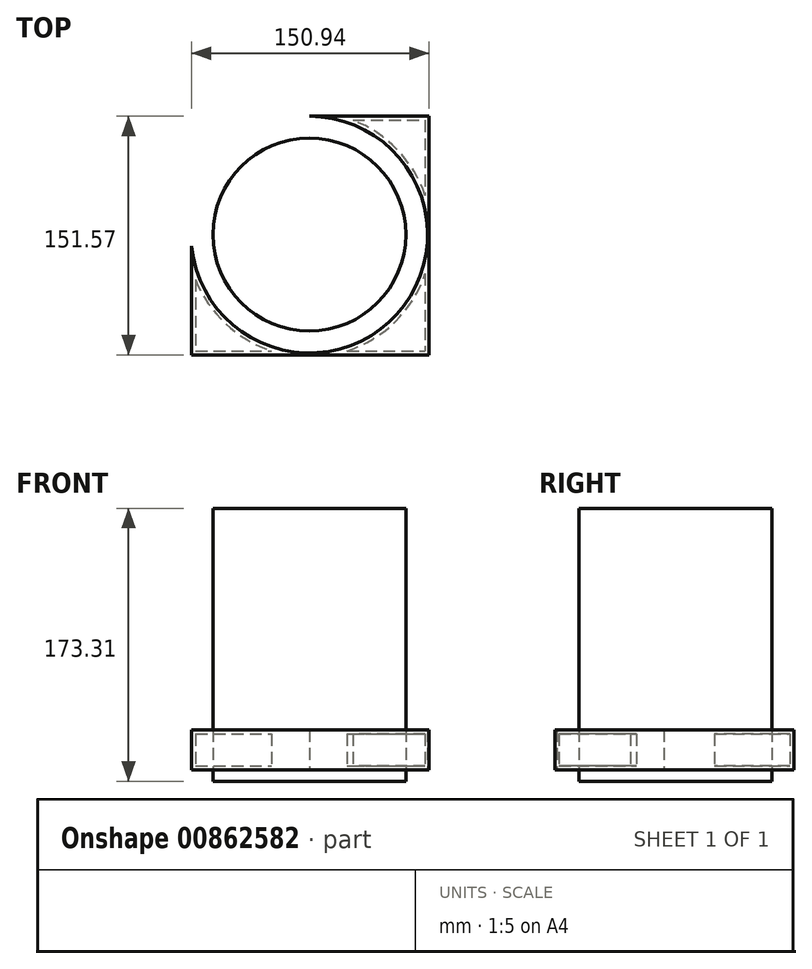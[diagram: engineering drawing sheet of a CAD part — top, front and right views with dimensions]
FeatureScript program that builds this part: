
annotation { "Feature Type Name" : "Feature", "Feature Type Description" : "" }
export const myFeature = defineFeature(function(context is Context, id is Id, definition is map)
    precondition{}
    {
        {
            var Q0;
            Q0=qCreatedBy(makeId("Top.planeOp"),FACE);
            var sketch = newSketch(context, id + "F0", { "sketchPlane" : qUnion([Q0])});
            skLineSegment(sketch, "E0.bottom", {"start": v(-74.79, 75.15) * mm, "end": v(76.15, 75.15) * mm});
            skLineSegment(sketch, "E0.top", {"start": v(-74.79, -76.42) * mm, "end": v(76.15, -76.42) * mm});
            skLineSegment(sketch, "E0.left", {"start": v(-74.79, 75.15) * mm, "end": v(-74.79, -76.42) * mm});
            skLineSegment(sketch, "E0.right", {"start": v(76.15, 75.15) * mm, "end": v(76.15, -76.42) * mm});
            skCircle(sketch, "E1", {"center": v(0, 0) * mm, "radius": 75.15 * mm});
            skSolve(sketch);
        }
        {
            var Q0;
            {var subQ0=sQuery(id+"F0.wireOp",EDGE,"E1");var subQ1=sQuery(id+"F0.wireOp",EDGE,"E0.left");var subQ2=makeQuery(id+"F0.imprint","INTERSECT",VERTEX,{"disambiguationData":[OD(0.0)],"derivedFrom":[subQ1,subQ0]});Q0=makeQuery(id+"F0.imprint","IMPRINT",FACE,{"disambiguationData":[TD([[makeQuery(id+"F0.imprint","IMPRINT",EDGE,{"disambiguationData":[TD([[subQ2,-1.0]])],"derivedFrom":subQ1}),1.0]])]});}
            extrude(context, id + "F1", {"entities" : qUnion([Q0]), "depth" : 25.4 * mm, "offsetDistance" : 25.4 * mm});
        }
        {
            var Q0;
            Q0=makeQuery(id+"F1.opExtrude","CAP_FACE",FACE,{"disambiguationData":[OSD([sQuery(id+"F0.wireOp",EDGE,"E0.left"),sQuery(id+"F0.wireOp",EDGE,"E1")])],"isStart":false});
            var sketch = newSketch(context, id + "F2", { "sketchPlane" : qUnion([Q0])});
            skCircle(sketch, "E2", {"center": v(0, 0) * mm, "radius": 61.24 * mm});
            skSolve(sketch);
        }
        {
            var Q0;
            Q0=makeQuery(id+"F2.imprint","IMPRINT",FACE,{"disambiguationData":[TD([[makeQuery(id+"F2.imprint","IMPRINT",EDGE,{"derivedFrom":sQuery(id+"F2.wireOp",EDGE,"E2")}),1.0]])]});
            extrude(context, id + "F3", {"entities" : qUnion([Q0]), "operationType" : NewBodyOperationType.ADD, "depth" : 140.76 * mm, "offsetDistance" : 25.4 * mm, "hasSecondDirection" : true, "secondDirectionOppositeDirection" : true, "secondDirectionDepth" : 32.55 * mm});
        }
        {
            var Q0;
            {var subQ0=sQuery(id+"F2.wireOp",EDGE,"E2");Q0=makeQuery(id+"F3.boolean.opBoolean","SPLIT",FACE,{"disambiguationData":[TD([makeQuery(id+"F3.opExtrude","CAP_FACE",FACE,{"disambiguationData":[OSD([subQ0])],"isStart":false})])],"derivedFrom":makeQuery(id+"F3.opExtrude","SWEPT_FACE",FACE,{"disambiguationData":[OSD([subQ0])]})});}
            var Q1;
            Q1=makeQuery(id+"F1.opExtrude","SWEPT_BODY",BODY,{"disambiguationData":[OSD([sQuery(id+"F0.wireOp",EDGE,"E0.left"),sQuery(id+"F0.wireOp",EDGE,"E1")])]});
            shell(context, id + "F4", {"isHollow" : true, "entities" : qUnion([Q0]), "parts" : qUnion([Q1]), "thickness" : 2.54 * mm});
        }
    });
